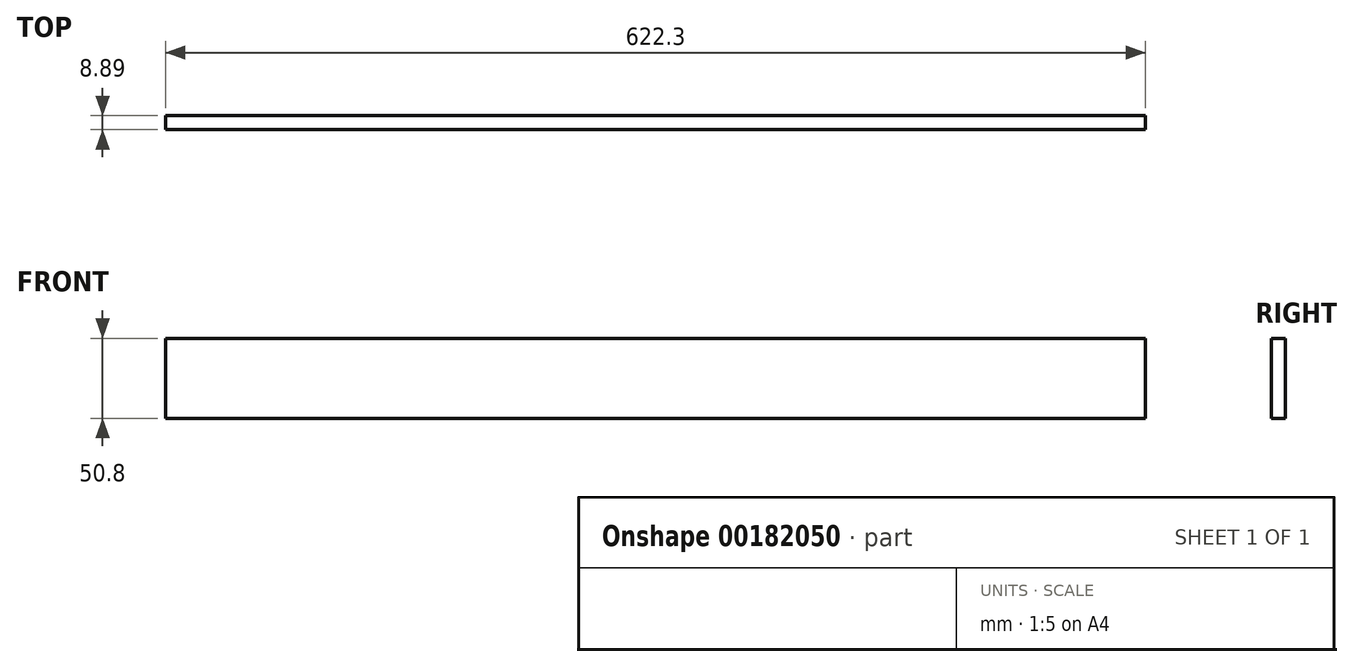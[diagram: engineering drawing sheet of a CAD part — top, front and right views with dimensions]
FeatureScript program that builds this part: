
annotation { "Feature Type Name" : "Feature", "Feature Type Description" : "" }
export const myFeature = defineFeature(function(context is Context, id is Id, definition is map)
    precondition{}
    {
        {
            var Q0;
            Q0=qCreatedBy(makeId("Front.planeOp"),FACE);
            var sketch = newSketch(context, id + "F0", { "sketchPlane" : qUnion([Q0])});
            skLineSegment(sketch, "E0", {"start": v(0, 0) * mm, "end": v(0, 50.8) * mm});
            skLineSegment(sketch, "E1", {"start": v(0, 50.8) * mm, "end": v(622.3, 50.8) * mm});
            skLineSegment(sketch, "E2", {"start": v(622.3, 50.8) * mm, "end": v(622.3, 0) * mm});
            skLineSegment(sketch, "E3", {"start": v(622.3, 0) * mm, "end": v(0, 0) * mm});
            skSolve(sketch);
        }
        {
            var Q0;
            Q0 = qSketchRegion(id + "F0", true);
            extrude(context, id + "F1", {"entities" : qUnion([Q0]), "depth" : 8.9 * mm});
        }
    });
